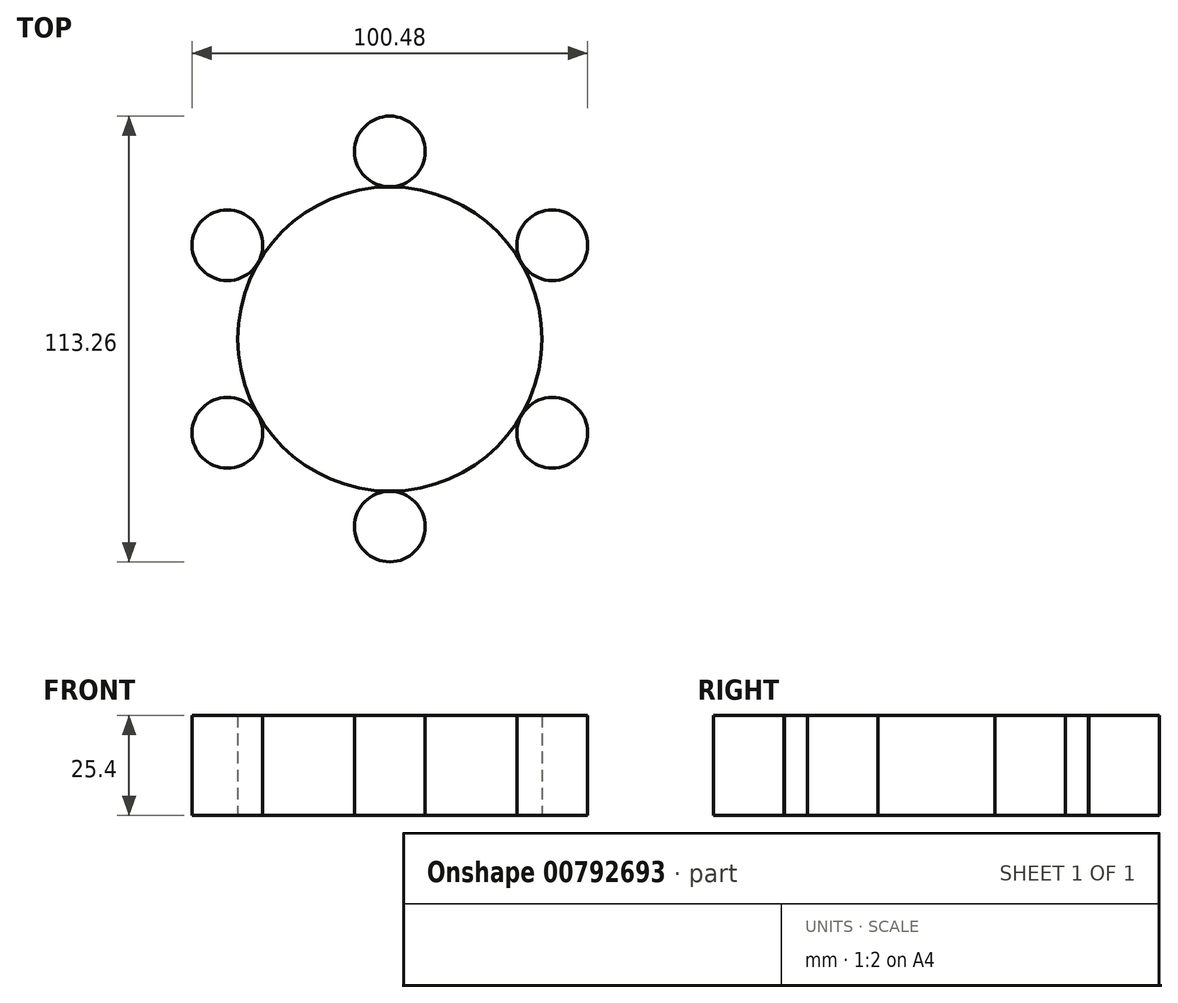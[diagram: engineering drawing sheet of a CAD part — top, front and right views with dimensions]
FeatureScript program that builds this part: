
annotation { "Feature Type Name" : "Feature", "Feature Type Description" : "" }
export const myFeature = defineFeature(function(context is Context, id is Id, definition is map)
    precondition{}
    {
        {
            var Q0;
            Q0=qCreatedBy(makeId("Top.planeOp"),FACE);
            var sketch = newSketch(context, id + "F0", { "sketchPlane" : qUnion([Q0])});
            skCircle(sketch, "E0", {"center": v(0, 0) * mm, "radius": 38.63 * mm});
            skCircle(sketch, "E1", {"center": v(0, 47.66) * mm, "radius": 8.97 * mm});
            skSolve(sketch);
        }
        {
            var Q0;
            Q0=makeQuery(id+"F0.imprint","IMPRINT",FACE,{"disambiguationData":[TD([[makeQuery(id+"F0.imprint","IMPRINT",EDGE,{"derivedFrom":sQuery(id+"F0.wireOp",EDGE,"E0")}),1.0]])]});
            var Q1;
            Q1=makeQuery(id+"F0.imprint","IMPRINT",FACE,{"disambiguationData":[TD([[makeQuery(id+"F0.imprint","IMPRINT",EDGE,{"derivedFrom":sQuery(id+"F0.wireOp",EDGE,"E1")}),1.0]])]});
            extrude(context, id + "F1", {"entities" : qUnion([Q0, Q1]), "depth" : 25.4 * mm, "offsetDistance" : 25.4 * mm});
        }
        {
            var Q0;
            Q0=makeQuery(id+"F1.opExtrude","SWEPT_BODY",BODY,{"disambiguationData":[OSD([sQuery(id+"F0.wireOp",EDGE,"E1")])]});
            var Q1;
            Q1=makeQuery(id+"F1.opExtrude","CAP_EDGE",EDGE,{"disambiguationData":[OSD([sQuery(id+"F0.wireOp",EDGE,"E0")])],"isStart":false});
            circularPattern(context, id + "F2", {"entities" : qUnion([Q0]), "axis" : qUnion([Q1]), "angle" : 360 * degree, "instanceCount" : 6, "equalSpace" : true});
        }
    });
